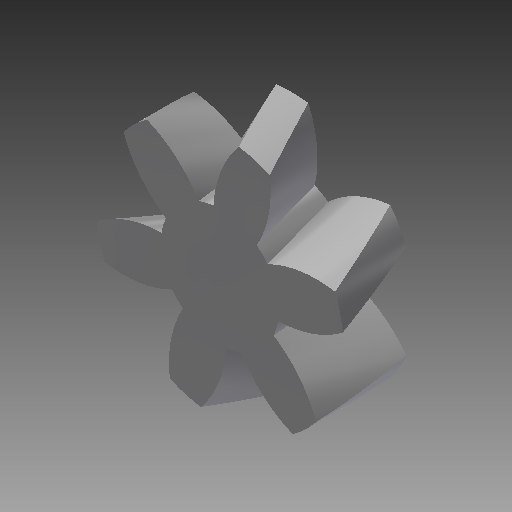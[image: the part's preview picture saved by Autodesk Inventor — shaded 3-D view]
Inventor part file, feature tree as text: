
AUTODESK INVENTOR PART (.ipt)
format: ipt  version: 2017 SP1 (Build 210196100, 196)  size: 278,528 bytes
history: native  units: mm (DEFAULTED — no unit token found)
features: plane x3, other x3, sketch x2, extrude x1
ambient origin geometry x8: Origin, YZ Plane, XZ Plane, XY Plane, X Axis, Y Axis, Z Axis, Center Point
bodies: Solid1 (feature_tree)
feature tree (9):
  extrude  "Extrusion1"  Depth=10.0mm TaperAngle=0.0deg
  plane  "Work Plane2"
  plane  "Work Plane8"
  plane  "Work Plane9"
  other  "Engrenage cylindrique"
  sketch  "Sketch1"  dims[d0=34.188431mm d1=10.0mm d2=0.0mm]
  sketch  "Sketch2"  dims[d3=26.24881mm d4=10.0mm d5=0.0mm d16=26.24881mm d17=0.0mm d34=30.0deg d39=0.0mm d41=0.0mm d43=26.24881mm d46=26.24881mm d47=0.0mm d48=0.0mm]
  other  "Srf1"
  other  "Diamètre primitif"
